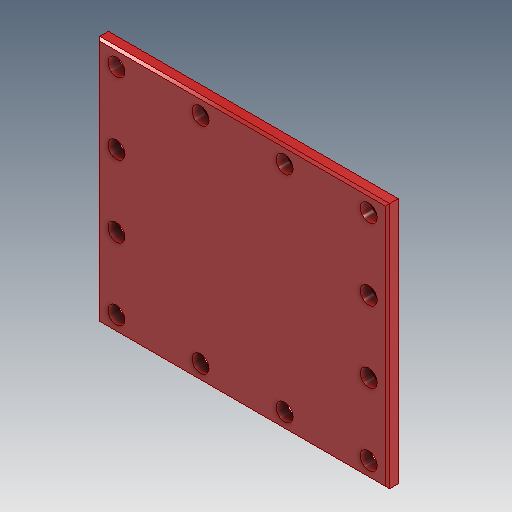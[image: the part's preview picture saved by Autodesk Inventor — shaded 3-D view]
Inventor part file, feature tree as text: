
AUTODESK INVENTOR PART (.ipt)
format: ipt  version: 2020.3 (Build 243373010, 373A)  size: 194,560 bytes
history: native  units: mm
features: sketch x3, extrude x3, chamfer x2, projected_geometry x2, hole x1
ambient origin geometry x8: Origin, YZ Plane, XZ Plane, XY Plane, X Axis, Y Axis, Z Axis, Center Point
bodies: Solid1 (feature_tree)
feature tree (11):
  sketch  "Sketch1"  dims[d0=270.0mm d1=230.0mm]
  extrude  "Extrusion1"  Depth=230.0mm
  extrude  "Extrusion2"  Depth=185.0mm
  chamfer  "Chamfer1"  Distance=15.0mm
  hole  "Hole1"  [1 undecoded]
  chamfer  "Chamfer2"  Distance=2.0mm Angle=45.0deg
  extrude  "Extrusion3"  Depth=10.0mm
  sketch  "Sketch2"  dims[d2=220.0mm d3=185.0mm d4=15.0mm d5=0.0mm]
  projected_geometry  "Projected Loop1"
  sketch  "Sketch3"  dims[d6=10.0mm d7=0.0mm d8=5.0mm d9=2.0mm d10=45.0deg d12=40.0mm d14=10.0mm d16=40.0mm d18=10.0mm d19=250.0mm d20=15.0mm d21=15.0mm d22=7.5mm d23=7.5mm d24=78.333333mm d25=215.0mm d26=66.666667mm d27=10.0mm d28=10.0mm d29=8.376mm d30=20.0mm d31=4.0mm d32=2.0mm d33=90.0deg d34=27.3mm d35=20.594885mm d36=2.0mm d37=2.0mm d38=45.0deg d39=16.0mm d40=40.0mm d42=78.333mm d43=10.0mm d45=10.0mm d47=40.0mm d49=66.667mm d50=10.0mm d52=10.0mm d54=40.0mm d56=78.333mm d57=10.0mm d59=10.0mm d61=30.0mm d63=66.667mm d64=10.0mm d66=10.0mm d68=10.0mm d69=0.0mm]
  projected_geometry  "Projected Loop2"
note: 1 required parameter value undecoded (feature->parameter linkage not recoverable at this tier; creation-order binding heuristic only, values carry confidence <= 0.55)
